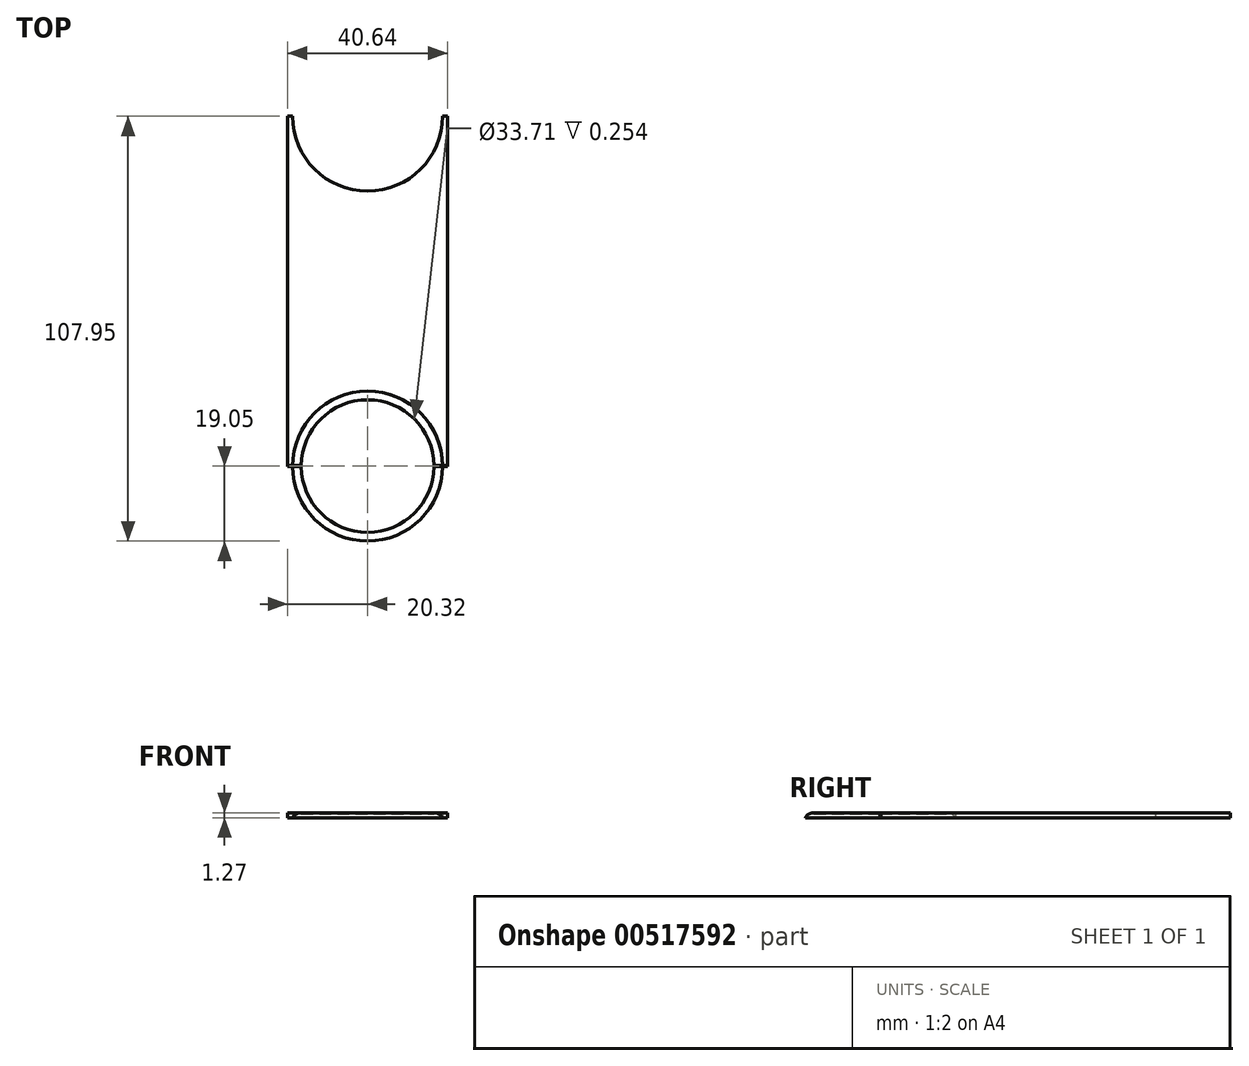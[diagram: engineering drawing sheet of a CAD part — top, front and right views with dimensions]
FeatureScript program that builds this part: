
annotation { "Feature Type Name" : "Feature", "Feature Type Description" : "" }
export const myFeature = defineFeature(function(context is Context, id is Id, definition is map)
    precondition{}
    {
        {
            var Q0;
            Q0=qCreatedBy(makeId("Top.planeOp"),FACE);
            var sketch = newSketch(context, id + "F0", { "sketchPlane" : qUnion([Q0])});
            skArc(sketch, "E0", {"start": v(-19.05, -0.13) * mm, "mid": v(0, -19.05) * mm, "end": v(19.05, -0.13) * mm});
            skLineSegment(sketch, "E1", {"start": v(-20.32, 0) * mm, "end": v(-20.32, 0.13) * mm});
            skLineSegment(sketch, "E2", {"start": v(-19.05, 0.13) * mm, "end": v(-20.32, 0.13) * mm});
            skLineSegment(sketch, "E3.MirrorCS", {"start": v(-20.32, 0) * mm, "end": v(-20.32, -0.13) * mm});
            skLineSegment(sketch, "E4.MirrorCS", {"start": v(-19.05, -0.13) * mm, "end": v(-20.32, -0.13) * mm});
            skLineSegment(sketch, "E5.MirrorCS", {"start": v(20.32, 0) * mm, "end": v(20.32, -0.13) * mm});
            skLineSegment(sketch, "E6.MirrorCS", {"start": v(20.32, 0) * mm, "end": v(20.32, 0.13) * mm});
            skLineSegment(sketch, "E7.MirrorCS", {"start": v(19.05, 0.13) * mm, "end": v(20.32, 0.13) * mm});
            skLineSegment(sketch, "E8.MirrorCS", {"start": v(19.05, -0.13) * mm, "end": v(20.32, -0.13) * mm});
            skArc(sketch, "E9.trimOffspring", {"start": v(19.05, 0.13) * mm, "mid": v(0, 19.05) * mm, "end": v(-19.05, 0.13) * mm});
            skCircle(sketch, "E10", {"center": v(0, 0) * mm, "radius": 16.85 * mm});
            skSolve(sketch);
        }
        {
            var Q0;
            Q0=qCreatedBy(makeId("Top.planeOp"),FACE);
            var sketch = newSketch(context, id + "F1", { "sketchPlane" : qUnion([Q0])});
            skArc(sketch, "E11", {"start": v(19.05, 0) * mm, "mid": v(0, 19.05) * mm, "end": v(-19.05, 0) * mm});
            skPoint(sketch, "E12.endSnap0", {"position": v(-19.05, 0) * mm});
            skPoint(sketch, "E13.endSnap0", {"position": v(19.05, 0) * mm});
            skArc(sketch, "E14", {"start": v(-19.05, 88.9) * mm, "mid": v(0, 69.85) * mm, "end": v(19.05, 88.9) * mm});
            skLineSegment(sketch, "E15", {"start": v(19.05, 88.9) * mm, "end": v(20.32, 88.9) * mm});
            skLineSegment(sketch, "E16", {"start": v(20.32, 88.9) * mm, "end": v(20.32, 0) * mm});
            skLineSegment(sketch, "E17", {"start": v(20.32, 0) * mm, "end": v(19.05, 0) * mm});
            skLineSegment(sketch, "E18", {"start": v(-19.05, 88.9) * mm, "end": v(-20.32, 88.9) * mm});
            skLineSegment(sketch, "E19", {"start": v(-20.32, 88.9) * mm, "end": v(-20.32, 0) * mm});
            skLineSegment(sketch, "E20", {"start": v(-20.32, 0) * mm, "end": v(-19.05, 0) * mm});
            skSolve(sketch);
        }
        {
            var Q0;
            Q0=makeQuery(id+"F0.imprint","IMPRINT",FACE,{"disambiguationData":[TD([[makeQuery(id+"F0.imprint","IMPRINT",EDGE,{"derivedFrom":sQuery(id+"F0.wireOp",EDGE,"E0")}),1.0]])]});
            extrude(context, id + "F2", {"entities" : qUnion([Q0]), "depth" : 1.27 * mm, "offsetDistance" : 25.4 * mm});
        }
        {
            var Q0;
            Q0=makeQuery(id+"F2.opExtrude","CAP_EDGE",EDGE,{"disambiguationData":[OSD([sQuery(id+"F0.wireOp",EDGE,"E9.trimOffspring")])],"isStart":false});
            fillet(context, id + "F3", {"entities" : qUnion([Q0]), "radius" : 2.54 * mm, "tangentPropagation" : true, "allowEdgeOverflow" : false});
        }
        {
            var Q0;
            Q0=makeQuery(id+"F2.opExtrude","CAP_EDGE",EDGE,{"disambiguationData":[OSD([sQuery(id+"F0.wireOp",EDGE,"E0")])],"isStart":false});
            fillet(context, id + "F4", {"entities" : qUnion([Q0]), "radius" : 2.54 * mm, "tangentPropagation" : true, "allowEdgeOverflow" : false});
        }
        {
            var Q0;
            Q0=makeQuery(id+"F0.imprint","IMPRINT",FACE,{"disambiguationData":[TD([[makeQuery(id+"F0.imprint","IMPRINT",EDGE,{"derivedFrom":sQuery(id+"F0.wireOp",EDGE,"E10")}),1.0]])]});
            extrude(context, id + "F5", {"entities" : qUnion([Q0]), "operationType" : NewBodyOperationType.ADD, "depth" : 1.02 * mm, "offsetDistance" : 25.4 * mm});
        }
        {
            var Q0;
            Q0 = qSketchRegion(id + "F1", true);
            extrude(context, id + "F6", {"entities" : qUnion([Q0]), "depth" : 1.27 * mm, "offsetDistance" : 25.4 * mm});
        }
    });
